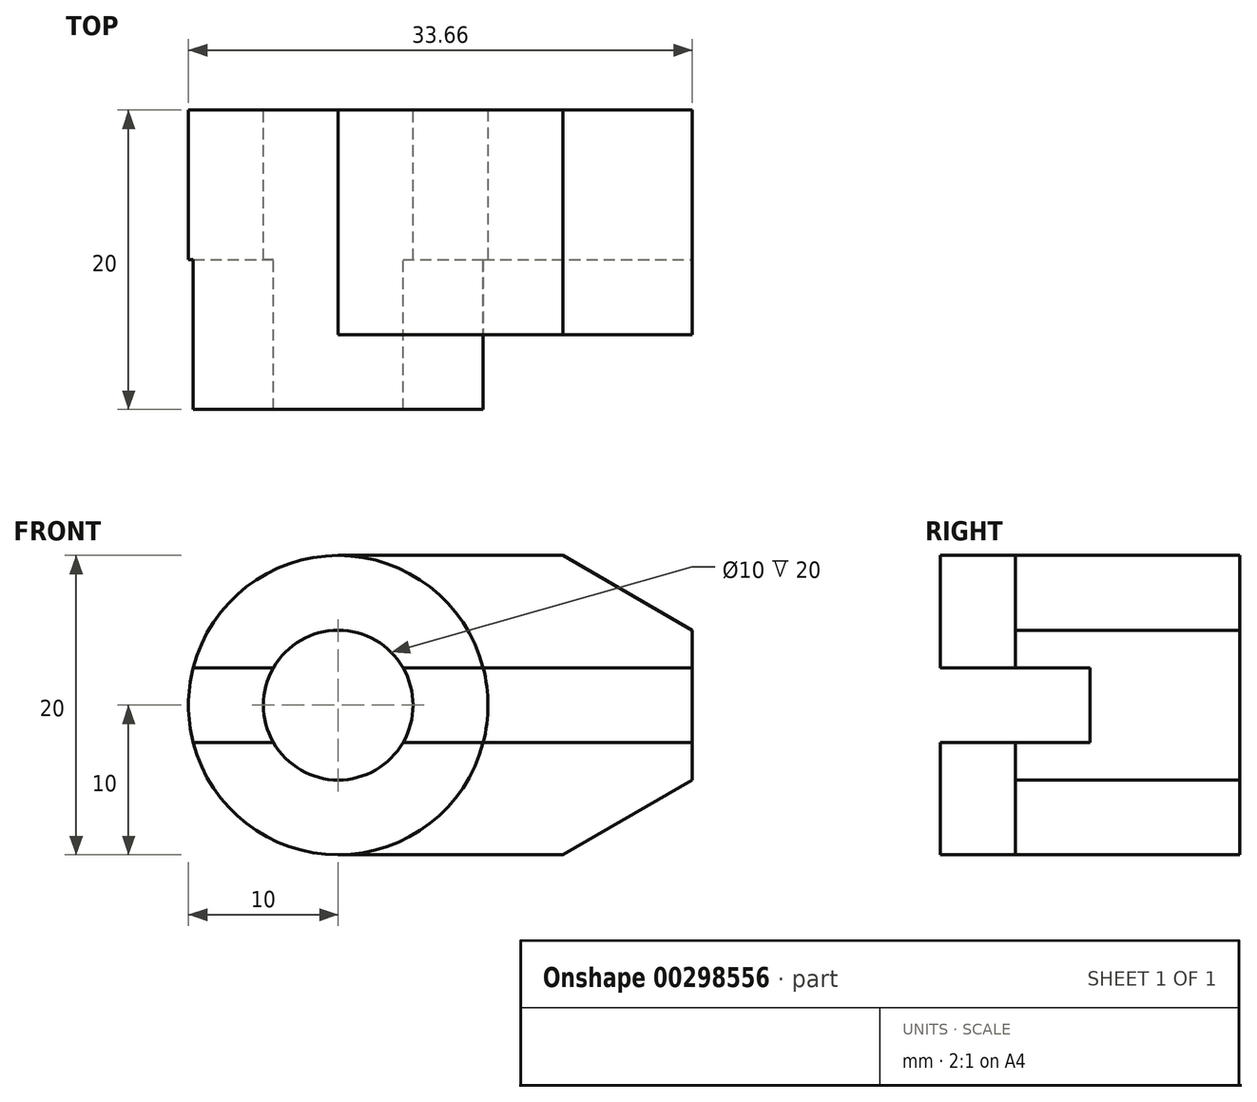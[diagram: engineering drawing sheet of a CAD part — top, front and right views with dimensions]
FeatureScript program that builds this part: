
annotation { "Feature Type Name" : "Feature", "Feature Type Description" : "" }
export const myFeature = defineFeature(function(context is Context, id is Id, definition is map)
    precondition{}
    {
        {
            var Q0;
            Q0=qCreatedBy(makeId("Front.planeOp"),FACE);
            var sketch = newSketch(context, id + "F0", { "sketchPlane" : qUnion([Q0])});
            skCircle(sketch, "E0", {"center": v(0, 0) * mm, "radius": 10 * mm});
            skCircle(sketch, "E1", {"center": v(0, 0) * mm, "radius": 5 * mm});
            skSolve(sketch);
        }
        {
            var Q0;
            Q0 = qSketchRegion(id + "F0", true);
            extrude(context, id + "F1", {"entities" : qUnion([Q0]), "depth" : 20 * mm});
        }
        {
            var Q0;
            Q0=makeQuery(id+"F1.opExtrude","CAP_FACE",FACE,{"disambiguationData":[OSD([sQuery(id+"F0.wireOp",EDGE,"E0"),sQuery(id+"F0.wireOp",EDGE,"E1")])],"isStart":false});
            var sketch = newSketch(context, id + "F2", { "sketchPlane" : qUnion([Q0])});
            skLineSegment(sketch, "E2", {"start": v(0, 10) * mm, "end": v(15, 10) * mm});
            skLineSegment(sketch, "E3", {"start": v(15, 10) * mm, "end": v(15, -10) * mm});
            skLineSegment(sketch, "E4", {"start": v(15, -10) * mm, "end": v(0, -10) * mm});
            skLineSegment(sketch, "E5", {"start": v(15, 10) * mm, "end": v(23.66, 5) * mm});
            skLineSegment(sketch, "E6", {"start": v(23.66, 5) * mm, "end": v(23.66, -5) * mm});
            skLineSegment(sketch, "E7", {"start": v(23.66, -5) * mm, "end": v(15, -10) * mm});
            skSolve(sketch);
        }
        {
            var Q0;
            Q0=makeQuery(id+"F2.imprint","IMPRINT",FACE,{"disambiguationData":[TD([[makeQuery(id+"F2.imprint","IMPRINT",EDGE,{"derivedFrom":sQuery(id+"F2.wireOp",EDGE,"E3")}),1.0]])]});
            var Q1;
            {var subQ0=sQuery(id+"F2.wireOp",EDGE,"E2");Q1=makeQuery(id+"F2.imprint","IMPRINT",FACE,{"disambiguationData":[TD([[makeQuery(id+"F2.imprint","IMPRINT",EDGE,{"derivedFrom":subQ0}),-1.0]])]});}
            extrude(context, id + "F3", {"entities" : qUnion([Q0, Q1]), "oppositeDirection" : true, "depth" : 20 * mm, "hasSecondDirection" : true, "secondDirectionOppositeDirection" : true, "secondDirectionDepth" : 5 * mm});
        }
        {
            var Q0;
            Q0=makeQuery(id+"F3.opExtrude","SWEPT_FACE",FACE,{"disambiguationData":[OSD([sQuery(id+"F2.wireOp",EDGE,"E6")])]});
            var sketch = newSketch(context, id + "F4", { "sketchPlane" : qUnion([Q0])});
            skLineSegment(sketch, "E8.bottom", {"start": v(-20, 2.5) * mm, "end": v(-10, 2.5) * mm});
            skLineSegment(sketch, "E8.top", {"start": v(-20, -2.5) * mm, "end": v(-10, -2.5) * mm});
            skLineSegment(sketch, "E8.left", {"start": v(-20, 2.5) * mm, "end": v(-20, -2.5) * mm});
            skLineSegment(sketch, "E8.right", {"start": v(-10, 2.5) * mm, "end": v(-10, -2.5) * mm});
            skSolve(sketch);
        }
        {
            var Q0;
            {var subQ0=sQuery(id+"F4.wireOp",EDGE,"E8.right");Q0=makeQuery(id+"F4.imprint","IMPRINT",FACE,{"disambiguationData":[TD([[makeQuery(id+"F4.imprint","IMPRINT",EDGE,{"derivedFrom":subQ0}),-1.0]])]});}
            var Q1;
            {var subQ0=sQuery(id+"F4.wireOp",EDGE,"E8.left");Q1=makeQuery(id+"F4.imprint","IMPRINT",FACE,{"disambiguationData":[TD([[makeQuery(id+"F4.imprint","IMPRINT",EDGE,{"derivedFrom":subQ0}),1.0]])]});}
            extrude(context, id + "F5", {"entities" : qUnion([Q0, Q1]), "operationType" : NewBodyOperationType.REMOVE, "endBound" : BoundingType.THROUGH_ALL, "oppositeDirection" : true, "depth" : 25 * mm});
        }
    });
